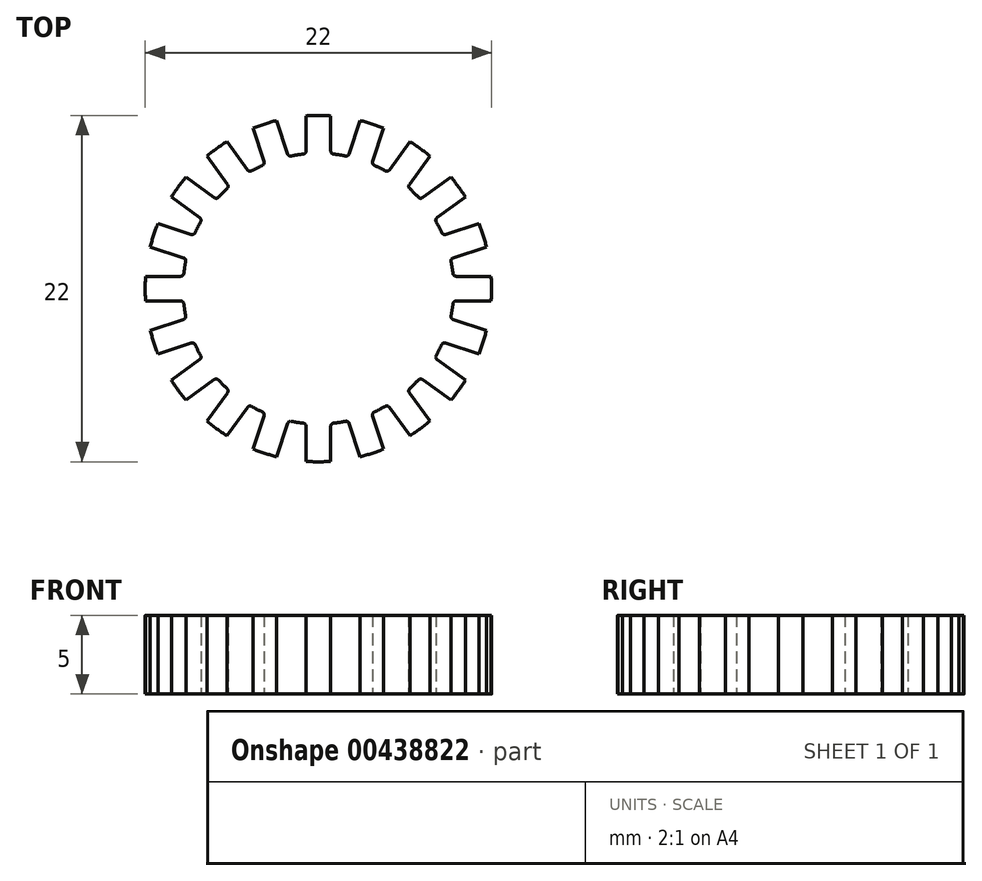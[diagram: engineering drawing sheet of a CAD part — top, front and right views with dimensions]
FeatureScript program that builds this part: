
annotation { "Feature Type Name" : "Feature", "Feature Type Description" : "" }
export const myFeature = defineFeature(function(context is Context, id is Id, definition is map)
    precondition{}
    {
        {
            var Q0;
            Q0=qCreatedBy(makeId("Top.planeOp"),FACE);
            var sketch = newSketch(context, id + "F0", { "sketchPlane" : qUnion([Q0])});
            skArc(sketch, "E0", {"start": v(0.4, 16) * mm, "mid": v(0, 16) * mm, "end": v(-0.4, 16) * mm});
            skCircle(sketch, "E1", {"center": v(0, 0) * mm, "radius": 15 * mm, "construction": true});
            skArc(sketch, "E2", {"start": v(-0.96, 8.55) * mm, "mid": v(-1.97, 8.37) * mm, "end": v(-2.94, 8.08) * mm});
            skLineSegment(sketch, "E3", {"start": v(-0.79, 8.74) * mm, "end": v(-0.79, 10.97) * mm});
            skLineSegment(sketch, "E4", {"start": v(0.79, 8.74) * mm, "end": v(0.79, 10.97) * mm});
            skLineSegment(sketch, "E5", {"start": v(0, 0) * mm, "end": v(5.13, 14.1) * mm, "construction": true});
            skArc(sketch, "E6.trimOffspring", {"start": v(-0.4, 16) * mm, "mid": v(-0.61, 15.5) * mm, "end": v(-0.79, 14.98) * mm});
            skLineSegment(sketch, "E7", {"start": v(0, 0) * mm, "end": v(-2.94, 8.08) * mm, "construction": true});
            skPoint(sketch, "E8", {"position": v(0.79, 14.98) * mm});
            skArc(sketch, "E9.trimOffspring", {"start": v(0.79, 14.98) * mm, "mid": v(0.61, 15.5) * mm, "end": v(0.4, 16) * mm});
            skPoint(sketch, "E10.visualSharp", {"position": v(-0.79, 8.56) * mm});
            skArc(sketch, "E10.filletArc", {"start": v(-0.96, 8.55) * mm, "mid": v(-0.84, 8.61) * mm, "end": v(-0.79, 8.74) * mm});
            skPoint(sketch, "E11.visualSharp", {"position": v(0.79, 8.56) * mm});
            skArc(sketch, "E11.filletArc", {"start": v(0.79, 8.74) * mm, "mid": v(0.84, 8.61) * mm, "end": v(0.96, 8.55) * mm});
            skArc(sketch, "E12.1.0", {"start": v(-3.56, 7.83) * mm, "mid": v(-3.46, 7.93) * mm, "end": v(-3.45, 8.07) * mm});
            skLineSegment(sketch, "E12.1.1", {"start": v(-3.45, 8.07) * mm, "end": v(-4.14, 10.2) * mm});
            skArc(sketch, "E12.1.2", {"start": v(-5.32, 15.1) * mm, "mid": v(-5.37, 14.55) * mm, "end": v(-5.38, 14) * mm});
            skArc(sketch, "E12.1.3", {"start": v(-4.57, 15.33) * mm, "mid": v(-4.94, 15.22) * mm, "end": v(-5.32, 15.1) * mm});
            skArc(sketch, "E12.1.4", {"start": v(-3.88, 14.49) * mm, "mid": v(-4.2, 14.93) * mm, "end": v(-4.57, 15.33) * mm});
            skLineSegment(sketch, "E12.1.5", {"start": v(-1.96, 8.56) * mm, "end": v(-2.64, 10.68) * mm});
            skArc(sketch, "E12.1.6", {"start": v(-1.96, 8.56) * mm, "mid": v(-1.87, 8.45) * mm, "end": v(-1.72, 8.43) * mm});
            skArc(sketch, "E12.2.0", {"start": v(-5.8, 6.35) * mm, "mid": v(-5.74, 6.48) * mm, "end": v(-5.78, 6.61) * mm});
            skLineSegment(sketch, "E12.2.1", {"start": v(-5.78, 6.61) * mm, "end": v(-6.5, 7.6) * mm});
            skArc(sketch, "E12.2.2", {"start": v(-9.72, 12.7) * mm, "mid": v(-9.6, 12.18) * mm, "end": v(-9.44, 11.66) * mm});
            skArc(sketch, "E12.2.3", {"start": v(-9.08, 13.17) * mm, "mid": v(-9.4, 12.94) * mm, "end": v(-9.72, 12.7) * mm});
            skArc(sketch, "E12.2.4", {"start": v(-8.17, 12.58) * mm, "mid": v(-8.61, 12.9) * mm, "end": v(-9.08, 13.17) * mm});
            skLineSegment(sketch, "E12.2.5", {"start": v(-4.5, 7.54) * mm, "end": v(-5.81, 9.34) * mm});
            skArc(sketch, "E12.2.6", {"start": v(-4.5, 7.54) * mm, "mid": v(-4.39, 7.46) * mm, "end": v(-4.24, 7.48) * mm});
            skArc(sketch, "E12.3.0", {"start": v(-7.48, 4.24) * mm, "mid": v(-7.46, 4.39) * mm, "end": v(-7.54, 4.5) * mm});
            skLineSegment(sketch, "E12.3.1", {"start": v(-7.54, 4.5) * mm, "end": v(-9.34, 5.81) * mm});
            skArc(sketch, "E12.3.2", {"start": v(-13.17, 9.08) * mm, "mid": v(-12.9, 8.61) * mm, "end": v(-12.58, 8.17) * mm});
            skArc(sketch, "E12.3.3", {"start": v(-12.7, 9.72) * mm, "mid": v(-12.94, 9.4) * mm, "end": v(-13.17, 9.08) * mm});
            skArc(sketch, "E12.3.4", {"start": v(-11.66, 9.44) * mm, "mid": v(-12.18, 9.6) * mm, "end": v(-12.7, 9.72) * mm});
            skLineSegment(sketch, "E12.3.5", {"start": v(-6.61, 5.78) * mm, "end": v(-8.41, 7.08) * mm});
            skArc(sketch, "E12.3.6", {"start": v(-6.61, 5.78) * mm, "mid": v(-6.48, 5.74) * mm, "end": v(-6.35, 5.8) * mm});
            skArc(sketch, "E12.4.0", {"start": v(-8.43, 1.72) * mm, "mid": v(-8.45, 1.87) * mm, "end": v(-8.56, 1.96) * mm});
            skLineSegment(sketch, "E12.4.1", {"start": v(-8.56, 1.96) * mm, "end": v(-9.72, 2.33) * mm});
            skArc(sketch, "E12.4.2", {"start": v(-15.33, 4.57) * mm, "mid": v(-14.93, 4.2) * mm, "end": v(-14.49, 3.88) * mm});
            skArc(sketch, "E12.4.3", {"start": v(-15.1, 5.32) * mm, "mid": v(-15.22, 4.94) * mm, "end": v(-15.33, 4.57) * mm});
            skArc(sketch, "E12.4.4", {"start": v(-14, 5.38) * mm, "mid": v(-14.55, 5.37) * mm, "end": v(-15.1, 5.32) * mm});
            skLineSegment(sketch, "E12.4.5", {"start": v(-8.07, 3.45) * mm, "end": v(-10.2, 4.14) * mm});
            skArc(sketch, "E12.4.6", {"start": v(-8.07, 3.45) * mm, "mid": v(-7.93, 3.46) * mm, "end": v(-7.83, 3.56) * mm});
            skArc(sketch, "E12.5.0", {"start": v(-8.55, -0.96) * mm, "mid": v(-8.61, -0.84) * mm, "end": v(-8.74, -0.79) * mm});
            skLineSegment(sketch, "E12.5.1", {"start": v(-8.74, -0.79) * mm, "end": v(-14.98, -0.79) * mm});
            skArc(sketch, "E12.5.2", {"start": v(-16, -0.4) * mm, "mid": v(-15.5, -0.61) * mm, "end": v(-14.98, -0.79) * mm});
            skArc(sketch, "E12.5.3", {"start": v(-16, 0.4) * mm, "mid": v(-16, 0) * mm, "end": v(-16, -0.4) * mm});
            skArc(sketch, "E12.5.4", {"start": v(-14.98, 0.79) * mm, "mid": v(-15.5, 0.61) * mm, "end": v(-16, 0.4) * mm});
            skLineSegment(sketch, "E12.5.5", {"start": v(-8.74, 0.79) * mm, "end": v(-10.97, 0.79) * mm});
            skArc(sketch, "E12.5.6", {"start": v(-8.74, 0.79) * mm, "mid": v(-8.61, 0.84) * mm, "end": v(-8.55, 0.96) * mm});
            skArc(sketch, "E12.6.0", {"start": v(-7.83, -3.56) * mm, "mid": v(-7.93, -3.46) * mm, "end": v(-8.07, -3.45) * mm});
            skLineSegment(sketch, "E12.6.1", {"start": v(-8.07, -3.45) * mm, "end": v(-10.2, -4.14) * mm});
            skArc(sketch, "E12.6.2", {"start": v(-15.1, -5.32) * mm, "mid": v(-14.55, -5.37) * mm, "end": v(-14, -5.38) * mm});
            skArc(sketch, "E12.6.3", {"start": v(-15.33, -4.57) * mm, "mid": v(-15.22, -4.94) * mm, "end": v(-15.1, -5.32) * mm});
            skArc(sketch, "E12.6.4", {"start": v(-14.49, -3.88) * mm, "mid": v(-14.93, -4.2) * mm, "end": v(-15.33, -4.57) * mm});
            skLineSegment(sketch, "E12.6.5", {"start": v(-8.56, -1.96) * mm, "end": v(-10.68, -2.64) * mm});
            skArc(sketch, "E12.6.6", {"start": v(-8.56, -1.96) * mm, "mid": v(-8.45, -1.87) * mm, "end": v(-8.43, -1.72) * mm});
            skArc(sketch, "E12.7.0", {"start": v(-6.35, -5.8) * mm, "mid": v(-6.48, -5.74) * mm, "end": v(-6.61, -5.78) * mm});
            skLineSegment(sketch, "E12.7.1", {"start": v(-6.61, -5.78) * mm, "end": v(-11.66, -9.44) * mm});
            skArc(sketch, "E12.7.2", {"start": v(-12.7, -9.72) * mm, "mid": v(-12.18, -9.6) * mm, "end": v(-11.66, -9.44) * mm});
            skArc(sketch, "E12.7.3", {"start": v(-13.17, -9.08) * mm, "mid": v(-12.94, -9.4) * mm, "end": v(-12.7, -9.72) * mm});
            skArc(sketch, "E12.7.4", {"start": v(-12.58, -8.17) * mm, "mid": v(-12.9, -8.61) * mm, "end": v(-13.17, -9.08) * mm});
            skLineSegment(sketch, "E12.7.5", {"start": v(-7.54, -4.5) * mm, "end": v(-9.34, -5.81) * mm});
            skArc(sketch, "E12.7.6", {"start": v(-7.54, -4.5) * mm, "mid": v(-7.46, -4.39) * mm, "end": v(-7.48, -4.24) * mm});
            skArc(sketch, "E12.8.0", {"start": v(-4.24, -7.48) * mm, "mid": v(-4.39, -7.46) * mm, "end": v(-4.5, -7.54) * mm});
            skLineSegment(sketch, "E12.8.1", {"start": v(-4.5, -7.54) * mm, "end": v(-5.81, -9.34) * mm});
            skArc(sketch, "E12.8.2", {"start": v(-9.08, -13.17) * mm, "mid": v(-8.61, -12.9) * mm, "end": v(-8.17, -12.58) * mm});
            skArc(sketch, "E12.8.3", {"start": v(-9.72, -12.7) * mm, "mid": v(-9.4, -12.94) * mm, "end": v(-9.08, -13.17) * mm});
            skArc(sketch, "E12.8.4", {"start": v(-9.44, -11.66) * mm, "mid": v(-9.6, -12.18) * mm, "end": v(-9.72, -12.7) * mm});
            skLineSegment(sketch, "E12.8.5", {"start": v(-5.78, -6.61) * mm, "end": v(-9.44, -11.66) * mm});
            skArc(sketch, "E12.8.6", {"start": v(-5.78, -6.61) * mm, "mid": v(-5.74, -6.48) * mm, "end": v(-5.8, -6.35) * mm});
            skArc(sketch, "E12.9.0", {"start": v(-1.72, -8.43) * mm, "mid": v(-1.87, -8.45) * mm, "end": v(-1.96, -8.56) * mm});
            skLineSegment(sketch, "E12.9.1", {"start": v(-1.96, -8.56) * mm, "end": v(-2.64, -10.68) * mm});
            skArc(sketch, "E12.9.2", {"start": v(-4.57, -15.33) * mm, "mid": v(-4.2, -14.93) * mm, "end": v(-3.88, -14.49) * mm});
            skArc(sketch, "E12.9.3", {"start": v(-5.32, -15.1) * mm, "mid": v(-4.94, -15.22) * mm, "end": v(-4.57, -15.33) * mm});
            skArc(sketch, "E12.9.4", {"start": v(-5.38, -14) * mm, "mid": v(-5.37, -14.55) * mm, "end": v(-5.32, -15.1) * mm});
            skLineSegment(sketch, "E12.9.5", {"start": v(-3.45, -8.07) * mm, "end": v(-5.38, -14) * mm});
            skArc(sketch, "E12.9.6", {"start": v(-3.45, -8.07) * mm, "mid": v(-3.46, -7.93) * mm, "end": v(-3.56, -7.83) * mm});
            skArc(sketch, "E12.10.0", {"start": v(0.96, -8.55) * mm, "mid": v(0.84, -8.61) * mm, "end": v(0.79, -8.74) * mm});
            skLineSegment(sketch, "E12.10.1", {"start": v(0.79, -8.74) * mm, "end": v(0.79, -10.97) * mm});
            skArc(sketch, "E12.10.2", {"start": v(0.4, -16) * mm, "mid": v(0.61, -15.5) * mm, "end": v(0.79, -14.98) * mm});
            skArc(sketch, "E12.10.3", {"start": v(-0.4, -16) * mm, "mid": v(0, -16) * mm, "end": v(0.4, -16) * mm});
            skArc(sketch, "E12.10.4", {"start": v(-0.79, -14.98) * mm, "mid": v(-0.61, -15.5) * mm, "end": v(-0.4, -16) * mm});
            skLineSegment(sketch, "E12.10.5", {"start": v(-0.79, -8.74) * mm, "end": v(-0.79, -14.98) * mm});
            skArc(sketch, "E12.10.6", {"start": v(-0.79, -8.74) * mm, "mid": v(-0.84, -8.61) * mm, "end": v(-0.96, -8.55) * mm});
            skArc(sketch, "E12.11.0", {"start": v(3.56, -7.83) * mm, "mid": v(3.46, -7.93) * mm, "end": v(3.45, -8.07) * mm});
            skLineSegment(sketch, "E12.11.1", {"start": v(3.45, -8.07) * mm, "end": v(4.14, -10.2) * mm});
            skArc(sketch, "E12.11.2", {"start": v(5.32, -15.1) * mm, "mid": v(5.37, -14.55) * mm, "end": v(5.38, -14) * mm});
            skArc(sketch, "E12.11.3", {"start": v(4.57, -15.33) * mm, "mid": v(4.94, -15.22) * mm, "end": v(5.32, -15.1) * mm});
            skArc(sketch, "E12.11.4", {"start": v(3.88, -14.49) * mm, "mid": v(4.2, -14.93) * mm, "end": v(4.57, -15.33) * mm});
            skLineSegment(sketch, "E12.11.5", {"start": v(1.96, -8.56) * mm, "end": v(3.88, -14.49) * mm});
            skArc(sketch, "E12.11.6", {"start": v(1.96, -8.56) * mm, "mid": v(1.87, -8.45) * mm, "end": v(1.72, -8.43) * mm});
            skArc(sketch, "E12.12.0", {"start": v(5.8, -6.35) * mm, "mid": v(5.74, -6.48) * mm, "end": v(5.78, -6.61) * mm});
            skLineSegment(sketch, "E12.12.1", {"start": v(5.78, -6.61) * mm, "end": v(7.08, -8.41) * mm});
            skArc(sketch, "E12.12.2", {"start": v(9.72, -12.7) * mm, "mid": v(9.6, -12.18) * mm, "end": v(9.44, -11.66) * mm});
            skArc(sketch, "E12.12.3", {"start": v(9.08, -13.17) * mm, "mid": v(9.4, -12.94) * mm, "end": v(9.72, -12.7) * mm});
            skArc(sketch, "E12.12.4", {"start": v(8.17, -12.58) * mm, "mid": v(8.61, -12.9) * mm, "end": v(9.08, -13.17) * mm});
            skLineSegment(sketch, "E12.12.5", {"start": v(4.5, -7.54) * mm, "end": v(8.17, -12.58) * mm});
            skArc(sketch, "E12.12.6", {"start": v(4.5, -7.54) * mm, "mid": v(4.39, -7.46) * mm, "end": v(4.24, -7.48) * mm});
            skArc(sketch, "E13.trimOffspring", {"start": v(-3.56, 7.83) * mm, "mid": v(-3.9, 7.66) * mm, "end": v(-4.24, 7.48) * mm});
            skArc(sketch, "E14.trimOffspring", {"start": v(2.94, 8.08) * mm, "mid": v(1.97, 8.37) * mm, "end": v(0.96, 8.55) * mm});
            skArc(sketch, "E15.trimOffspring", {"start": v(3.56, -7.83) * mm, "mid": v(8.6, 0) * mm, "end": v(3.56, 7.83) * mm});
            skArc(sketch, "E16.trimOffspring", {"start": v(-5.8, 6.35) * mm, "mid": v(-6.08, 6.08) * mm, "end": v(-6.35, 5.8) * mm});
            skArc(sketch, "E17.trimOffspring", {"start": v(-7.48, 4.24) * mm, "mid": v(-7.66, 3.9) * mm, "end": v(-7.83, 3.56) * mm});
            skArc(sketch, "E18.trimOffspring", {"start": v(-8.43, 1.72) * mm, "mid": v(-8.5, 1.35) * mm, "end": v(-8.55, 0.96) * mm});
            skArc(sketch, "E19.trimOffspring", {"start": v(-8.55, -0.96) * mm, "mid": v(-8.5, -1.35) * mm, "end": v(-8.43, -1.72) * mm});
            skArc(sketch, "E20.trimOffspring", {"start": v(-7.83, -3.56) * mm, "mid": v(-7.66, -3.9) * mm, "end": v(-7.48, -4.24) * mm});
            skArc(sketch, "E21.trimOffspring", {"start": v(-6.35, -5.8) * mm, "mid": v(-6.08, -6.08) * mm, "end": v(-5.8, -6.35) * mm});
            skArc(sketch, "E22.trimOffspring", {"start": v(-4.24, -7.48) * mm, "mid": v(-3.9, -7.66) * mm, "end": v(-3.56, -7.83) * mm});
            skArc(sketch, "E23.trimOffspring", {"start": v(-1.72, -8.43) * mm, "mid": v(-1.35, -8.5) * mm, "end": v(-0.96, -8.55) * mm});
            skArc(sketch, "E24.trimOffspring", {"start": v(0.96, -8.55) * mm, "mid": v(1.35, -8.5) * mm, "end": v(1.72, -8.43) * mm});
            skArc(sketch, "E25", {"start": v(-1.72, 8.43) * mm, "mid": v(2.34, -8.28) * mm, "end": v(-2.94, 8.08) * mm});
            skArc(sketch, "E26", {"start": v(2.94, 8.08) * mm, "mid": v(-2.34, -8.28) * mm, "end": v(1.72, 8.43) * mm});
            skArc(sketch, "E27.2.13.0", {"start": v(7.48, -4.24) * mm, "mid": v(7.46, -4.39) * mm, "end": v(7.54, -4.5) * mm});
            skLineSegment(sketch, "E27.4.13.0", {"start": v(7.54, -4.5) * mm, "end": v(9.34, -5.81) * mm});
            skArc(sketch, "E27.7.13.0", {"start": v(13.17, -9.08) * mm, "mid": v(12.9, -8.61) * mm, "end": v(12.58, -8.17) * mm});
            skArc(sketch, "E27.11.13.0", {"start": v(12.7, -9.72) * mm, "mid": v(12.94, -9.4) * mm, "end": v(13.17, -9.08) * mm});
            skArc(sketch, "E27.15.13.0", {"start": v(11.66, -9.44) * mm, "mid": v(12.18, -9.6) * mm, "end": v(12.7, -9.72) * mm});
            skLineSegment(sketch, "E27.19.13.0", {"start": v(6.61, -5.78) * mm, "end": v(11.66, -9.44) * mm});
            skArc(sketch, "E27.22.13.0", {"start": v(6.61, -5.78) * mm, "mid": v(6.48, -5.74) * mm, "end": v(6.35, -5.8) * mm});
            skArc(sketch, "E27.2.14.0", {"start": v(8.43, -1.72) * mm, "mid": v(8.45, -1.87) * mm, "end": v(8.56, -1.96) * mm});
            skLineSegment(sketch, "E27.4.14.0", {"start": v(8.56, -1.96) * mm, "end": v(10.68, -2.64) * mm});
            skArc(sketch, "E27.7.14.0", {"start": v(15.33, -4.57) * mm, "mid": v(14.93, -4.2) * mm, "end": v(14.49, -3.88) * mm});
            skArc(sketch, "E27.11.14.0", {"start": v(15.1, -5.32) * mm, "mid": v(15.22, -4.94) * mm, "end": v(15.33, -4.57) * mm});
            skArc(sketch, "E27.15.14.0", {"start": v(14, -5.38) * mm, "mid": v(14.55, -5.37) * mm, "end": v(15.1, -5.32) * mm});
            skLineSegment(sketch, "E27.19.14.0", {"start": v(8.07, -3.45) * mm, "end": v(14, -5.38) * mm});
            skArc(sketch, "E27.22.14.0", {"start": v(8.07, -3.45) * mm, "mid": v(7.93, -3.46) * mm, "end": v(7.83, -3.56) * mm});
            skArc(sketch, "E27.2.15.0", {"start": v(8.55, 0.96) * mm, "mid": v(8.61, 0.84) * mm, "end": v(8.74, 0.79) * mm});
            skLineSegment(sketch, "E27.4.15.0", {"start": v(8.74, 0.79) * mm, "end": v(10.97, 0.79) * mm});
            skArc(sketch, "E27.7.15.0", {"start": v(16, 0.4) * mm, "mid": v(15.5, 0.61) * mm, "end": v(14.98, 0.79) * mm});
            skArc(sketch, "E27.11.15.0", {"start": v(16, -0.4) * mm, "mid": v(16, 0) * mm, "end": v(16, 0.4) * mm});
            skArc(sketch, "E27.15.15.0", {"start": v(14.98, -0.79) * mm, "mid": v(15.5, -0.61) * mm, "end": v(16, -0.4) * mm});
            skLineSegment(sketch, "E27.19.15.0", {"start": v(8.74, -0.79) * mm, "end": v(14.98, -0.79) * mm});
            skArc(sketch, "E27.22.15.0", {"start": v(8.74, -0.79) * mm, "mid": v(8.61, -0.84) * mm, "end": v(8.55, -0.96) * mm});
            skArc(sketch, "E27.2.16.0", {"start": v(7.83, 3.56) * mm, "mid": v(7.93, 3.46) * mm, "end": v(8.07, 3.45) * mm});
            skLineSegment(sketch, "E27.4.16.0", {"start": v(8.07, 3.45) * mm, "end": v(10.2, 4.14) * mm});
            skArc(sketch, "E27.7.16.0", {"start": v(15.1, 5.32) * mm, "mid": v(14.55, 5.37) * mm, "end": v(14, 5.38) * mm});
            skArc(sketch, "E27.11.16.0", {"start": v(15.33, 4.57) * mm, "mid": v(15.22, 4.94) * mm, "end": v(15.1, 5.32) * mm});
            skArc(sketch, "E27.15.16.0", {"start": v(14.49, 3.88) * mm, "mid": v(14.93, 4.2) * mm, "end": v(15.33, 4.57) * mm});
            skLineSegment(sketch, "E27.19.16.0", {"start": v(8.56, 1.96) * mm, "end": v(14.49, 3.88) * mm});
            skArc(sketch, "E27.22.16.0", {"start": v(8.56, 1.96) * mm, "mid": v(8.45, 1.87) * mm, "end": v(8.43, 1.72) * mm});
            skArc(sketch, "E27.2.17.0", {"start": v(6.35, 5.8) * mm, "mid": v(6.48, 5.74) * mm, "end": v(6.61, 5.78) * mm});
            skLineSegment(sketch, "E27.4.17.0", {"start": v(6.61, 5.78) * mm, "end": v(8.41, 7.08) * mm});
            skArc(sketch, "E27.7.17.0", {"start": v(12.7, 9.72) * mm, "mid": v(12.18, 9.6) * mm, "end": v(11.66, 9.44) * mm});
            skArc(sketch, "E27.11.17.0", {"start": v(13.17, 9.08) * mm, "mid": v(12.94, 9.4) * mm, "end": v(12.7, 9.72) * mm});
            skArc(sketch, "E27.15.17.0", {"start": v(12.58, 8.17) * mm, "mid": v(12.9, 8.61) * mm, "end": v(13.17, 9.08) * mm});
            skLineSegment(sketch, "E27.19.17.0", {"start": v(7.54, 4.5) * mm, "end": v(12.58, 8.17) * mm});
            skArc(sketch, "E27.22.17.0", {"start": v(7.54, 4.5) * mm, "mid": v(7.46, 4.39) * mm, "end": v(7.48, 4.24) * mm});
            skArc(sketch, "E27.2.18.0", {"start": v(4.24, 7.48) * mm, "mid": v(4.39, 7.46) * mm, "end": v(4.5, 7.54) * mm});
            skLineSegment(sketch, "E27.4.18.0", {"start": v(4.5, 7.54) * mm, "end": v(5.81, 9.34) * mm});
            skArc(sketch, "E27.7.18.0", {"start": v(9.08, 13.17) * mm, "mid": v(8.61, 12.9) * mm, "end": v(8.17, 12.58) * mm});
            skArc(sketch, "E27.11.18.0", {"start": v(9.72, 12.7) * mm, "mid": v(9.4, 12.94) * mm, "end": v(9.08, 13.17) * mm});
            skArc(sketch, "E27.15.18.0", {"start": v(9.44, 11.66) * mm, "mid": v(9.6, 12.18) * mm, "end": v(9.72, 12.7) * mm});
            skLineSegment(sketch, "E27.19.18.0", {"start": v(5.78, 6.61) * mm, "end": v(9.44, 11.66) * mm});
            skArc(sketch, "E27.22.18.0", {"start": v(5.78, 6.61) * mm, "mid": v(5.74, 6.48) * mm, "end": v(5.8, 6.35) * mm});
            skArc(sketch, "E27.2.19.0", {"start": v(1.72, 8.43) * mm, "mid": v(1.87, 8.45) * mm, "end": v(1.96, 8.56) * mm});
            skLineSegment(sketch, "E27.4.19.0", {"start": v(1.96, 8.56) * mm, "end": v(2.64, 10.68) * mm});
            skArc(sketch, "E27.7.19.0", {"start": v(4.57, 15.33) * mm, "mid": v(4.2, 14.93) * mm, "end": v(3.88, 14.49) * mm});
            skArc(sketch, "E27.11.19.0", {"start": v(5.32, 15.1) * mm, "mid": v(4.94, 15.22) * mm, "end": v(4.57, 15.33) * mm});
            skArc(sketch, "E27.15.19.0", {"start": v(5.38, 14) * mm, "mid": v(5.37, 14.55) * mm, "end": v(5.32, 15.1) * mm});
            skLineSegment(sketch, "E27.19.19.0", {"start": v(3.45, 8.07) * mm, "end": v(4.14, 10.2) * mm});
            skArc(sketch, "E27.22.19.0", {"start": v(3.45, 8.07) * mm, "mid": v(3.46, 7.93) * mm, "end": v(3.56, 7.83) * mm});
            skCircle(sketch, "E28", {"center": v(0, 0) * mm, "radius": 11 * mm, "construction": true});
            skCircle(sketch, "E29", {"center": v(0, 0) * mm, "radius": 10 * mm, "construction": true});
            skArc(sketch, "E30", {"start": v(-0.79, 10.97) * mm, "mid": v(0, 11) * mm, "end": v(0.79, 10.97) * mm});
            skPoint(sketch, "E31.orphan", {"position": v(-3.88, 14.49) * mm});
            skPoint(sketch, "E32.orphan", {"position": v(5.38, 14) * mm});
            skArc(sketch, "E33.1.0", {"start": v(-4.14, 10.2) * mm, "mid": v(-3.4, 10.46) * mm, "end": v(-2.64, 10.68) * mm});
            skArc(sketch, "E33.2.0", {"start": v(-7.08, 8.41) * mm, "mid": v(-6.47, 8.9) * mm, "end": v(-5.81, 9.34) * mm});
            skArc(sketch, "E33.3.0", {"start": v(-9.34, 5.81) * mm, "mid": v(-8.9, 6.47) * mm, "end": v(-8.41, 7.08) * mm});
            skArc(sketch, "E33.4.0", {"start": v(-10.68, 2.64) * mm, "mid": v(-10.46, 3.4) * mm, "end": v(-10.2, 4.14) * mm});
            skArc(sketch, "E33.5.0", {"start": v(-10.97, -0.79) * mm, "mid": v(-11, 0) * mm, "end": v(-10.97, 0.79) * mm});
            skArc(sketch, "E33.6.0", {"start": v(-10.2, -4.14) * mm, "mid": v(-10.46, -3.4) * mm, "end": v(-10.68, -2.64) * mm});
            skArc(sketch, "E33.7.0", {"start": v(-8.41, -7.08) * mm, "mid": v(-8.9, -6.47) * mm, "end": v(-9.34, -5.81) * mm});
            skArc(sketch, "E33.8.0", {"start": v(-5.81, -9.34) * mm, "mid": v(-6.47, -8.9) * mm, "end": v(-7.08, -8.41) * mm});
            skArc(sketch, "E33.9.0", {"start": v(-2.64, -10.68) * mm, "mid": v(-3.4, -10.46) * mm, "end": v(-4.14, -10.2) * mm});
            skArc(sketch, "E33.10.0", {"start": v(0.79, -10.97) * mm, "mid": v(0, -11) * mm, "end": v(-0.79, -10.97) * mm});
            skArc(sketch, "E33.11.0", {"start": v(4.14, -10.2) * mm, "mid": v(3.4, -10.46) * mm, "end": v(2.64, -10.68) * mm});
            skArc(sketch, "E33.12.0", {"start": v(7.08, -8.41) * mm, "mid": v(6.47, -8.9) * mm, "end": v(5.81, -9.34) * mm});
            skArc(sketch, "E33.13.0", {"start": v(9.34, -5.81) * mm, "mid": v(8.9, -6.47) * mm, "end": v(8.41, -7.08) * mm});
            skArc(sketch, "E33.14.0", {"start": v(10.68, -2.64) * mm, "mid": v(10.46, -3.4) * mm, "end": v(10.2, -4.14) * mm});
            skArc(sketch, "E33.15.0", {"start": v(10.97, 0.79) * mm, "mid": v(11, 0) * mm, "end": v(10.97, -0.79) * mm});
            skArc(sketch, "E33.16.0", {"start": v(10.2, 4.14) * mm, "mid": v(10.46, 3.4) * mm, "end": v(10.68, 2.64) * mm});
            skArc(sketch, "E33.17.0", {"start": v(8.41, 7.08) * mm, "mid": v(8.9, 6.47) * mm, "end": v(9.34, 5.81) * mm});
            skArc(sketch, "E33.18.0", {"start": v(5.81, 9.34) * mm, "mid": v(6.47, 8.9) * mm, "end": v(7.08, 8.41) * mm});
            skArc(sketch, "E33.19.0", {"start": v(2.64, 10.68) * mm, "mid": v(3.4, 10.46) * mm, "end": v(4.14, 10.2) * mm});
            skPoint(sketch, "E34.orphan", {"position": v(-8.17, 12.58) * mm});
            skPoint(sketch, "E35.orphan", {"position": v(-11.66, 9.44) * mm});
            skPoint(sketch, "E36.orphan", {"position": v(-14, 5.38) * mm});
            skPoint(sketch, "E37.orphan", {"position": v(-14.98, 0.79) * mm});
            skLineSegment(sketch, "E38", {"start": v(-9.72, 2.33) * mm, "end": v(-10.68, 2.64) * mm});
            skLineSegment(sketch, "E39", {"start": v(-7.08, 8.41) * mm, "end": v(-6.5, 7.6) * mm});
            skPoint(sketch, "E40.orphan", {"position": v(-14.49, -3.88) * mm});
            skPoint(sketch, "E41.orphan", {"position": v(-12.58, -8.17) * mm});
            skSolve(sketch);
        }
        {
            var Q0;
            Q0 = qSketchRegion(id + "F0", true);
            var Q1;
            Q1=makeQuery(id+"F0.imprint","IMPRINT",FACE,{"disambiguationData":[TD([[makeQuery(id+"F0.imprint","IMPRINT",EDGE,{"derivedFrom":sQuery(id+"F0.wireOp",EDGE,"8qkBZrjY-SoCQ-bmbn-ASt8-WrqOF0p5kUCL")}),1.0]])]});
            extrude(context, id + "F1", {"entities" : qUnion([Q0, Q1]), "depth" : 5 * mm});
        }
    });
